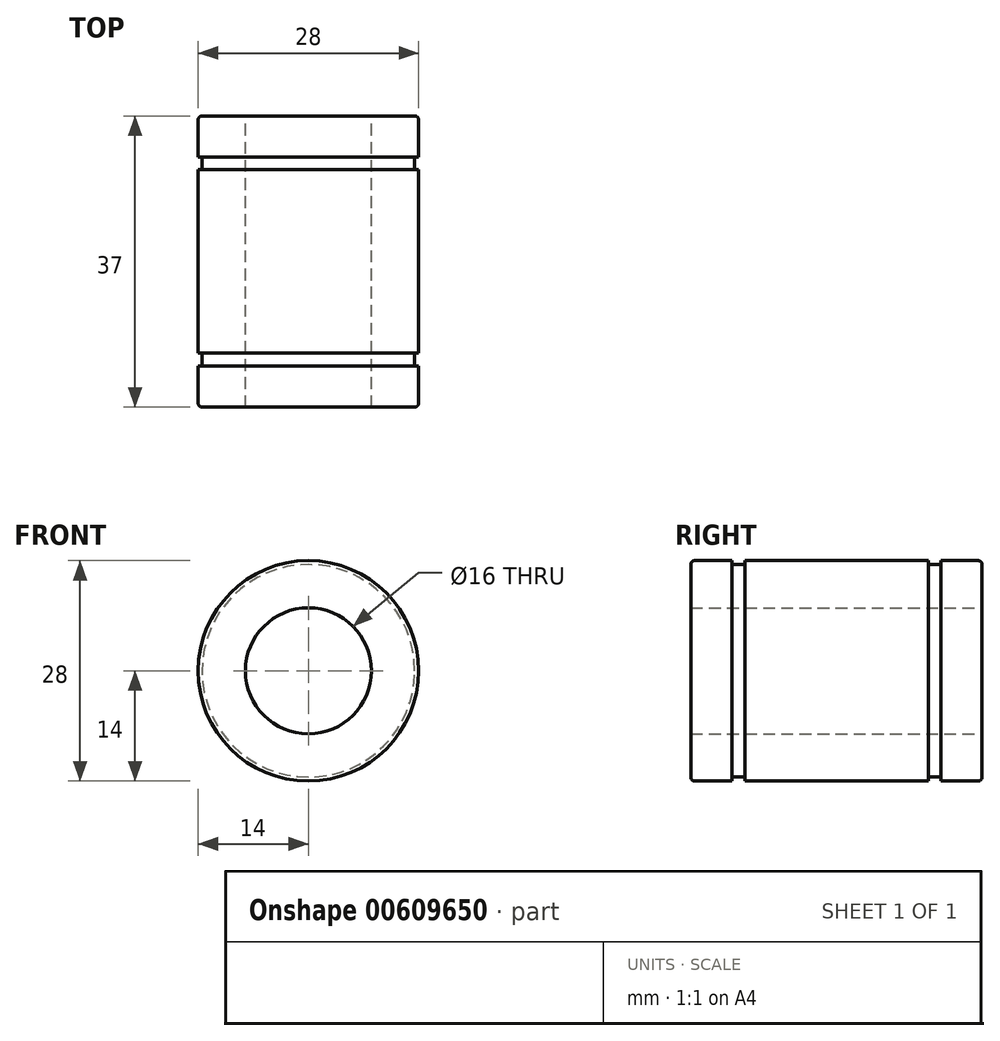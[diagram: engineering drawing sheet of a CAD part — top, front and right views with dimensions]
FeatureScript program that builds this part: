
annotation { "Feature Type Name" : "Feature", "Feature Type Description" : "" }
export const myFeature = defineFeature(function(context is Context, id is Id, definition is map)
    precondition{}
    {
        {
            var Q0;
            Q0=qCreatedBy(makeId("Front.planeOp"),FACE);
            var sketch = newSketch(context, id + "F0", { "sketchPlane" : qUnion([Q0])});
            skCircle(sketch, "E0", {"center": v(0, 0) * mm, "radius": 14 * mm});
            skCircle(sketch, "E1", {"center": v(0, 0) * mm, "radius": 8 * mm});
            skSolve(sketch);
        }
        {
            var Q0;
            Q0 = qSketchRegion(id + "F0", true);
            extrude(context, id + "F1", {"entities" : qUnion([Q0]), "depth" : 37 * mm, "offsetDistance" : 25 * mm, "symmetric" : true});
        }
        {
            var Q0;
            Q0=makeQuery(id+"F1.opExtrude","CAP_FACE",FACE,{"disambiguationData":[OSD([sQuery(id+"F0.wireOp",EDGE,"E0"),sQuery(id+"F0.wireOp",EDGE,"E1")])],"isStart":false});
            var sketch = newSketch(context, id + "F2", { "sketchPlane" : qUnion([Q0])});
            skCircle(sketch, "E2", {"center": v(0, 0) * mm, "radius": 13.5 * mm});
            skCircle(sketch, "E3", {"center": v(0, 0) * mm, "radius": 16.72 * mm});
            skSolve(sketch);
        }
        {
            var Q0;
            Q0 = qSketchRegion(id + "F2", true);
            extrude(context, id + "F3", {"entities" : qUnion([Q0]), "operationType" : NewBodyOperationType.REMOVE, "oppositeDirection" : true, "depth" : 6.85 * mm, "offsetDistance" : 25 * mm, "hasSecondDirection" : true, "secondDirectionOppositeDirection" : true, "secondDirectionDepth" : 5.25 * mm});
        }
        {
            var Q0;
            Q0=makeQuery(id+"F1.opExtrude","CAP_FACE",FACE,{"disambiguationData":[OSD([sQuery(id+"F0.wireOp",EDGE,"E0"),sQuery(id+"F0.wireOp",EDGE,"E1")])],"isStart":true});
            var sketch = newSketch(context, id + "F4", { "sketchPlane" : qUnion([Q0])});
            skCircle(sketch, "E4", {"center": v(0, 0) * mm, "radius": 13.5 * mm});
            skCircle(sketch, "E5", {"center": v(0, 0) * mm, "radius": 18.98 * mm});
            skSolve(sketch);
        }
        {
            var Q0;
            Q0=makeQuery(id+"F4.imprint","IMPRINT",FACE,{"disambiguationData":[TD([[makeQuery(id+"F4.imprint","IMPRINT",EDGE,{"derivedFrom":sQuery(id+"F4.wireOp",EDGE,"E4")}),-1.0]])]});
            extrude(context, id + "F5", {"entities" : qUnion([Q0]), "operationType" : NewBodyOperationType.REMOVE, "oppositeDirection" : true, "depth" : 6.85 * mm, "offsetDistance" : 25 * mm, "hasSecondDirection" : true, "secondDirectionOppositeDirection" : true, "secondDirectionDepth" : 5.25 * mm});
        }
        {
            var Q0;
            Q0=makeQuery(id+"F1.opExtrude","CAP_EDGE",EDGE,{"disambiguationData":[OSD([sQuery(id+"F0.wireOp",EDGE,"E0")])],"isStart":true});
            var Q1;
            Q1=makeQuery(id+"F1.opExtrude","CAP_EDGE",EDGE,{"disambiguationData":[OSD([sQuery(id+"F0.wireOp",EDGE,"E0")])],"isStart":false});
            fillet(context, id + "F6", {"entities" : qUnion([Q0, Q1]), "radius" : 0.5 * mm, "tangentPropagation" : true, "allowEdgeOverflow" : false});
        }
    });
